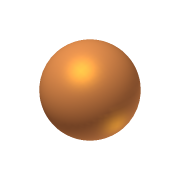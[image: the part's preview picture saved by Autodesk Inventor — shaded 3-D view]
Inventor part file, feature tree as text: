
AUTODESK INVENTOR PART (.ipt)
format: ipt  version: 2012 (Build 160160000, 160)  size: 130,560 bytes
history: native  units: in
note: dims shown in document units (in); Inventor stores cm internally (conversion verified against a paired STEP export)
features: revolve x1, sketch x1
ambient origin geometry x8: Origin, YZ Plane, XZ Plane, XY Plane, X Axis, Y Axis, Z Axis, Center Point
feature tree (2):
  revolve  "Revolution2"  [1 undecoded]
  sketch  "Sketch1"  dims[d0=3.975in d2=0.01in d3=90.0deg]
note: 1 required parameter value undecoded (feature->parameter linkage not recoverable at this tier; creation-order binding heuristic only, values carry confidence <= 0.55)
